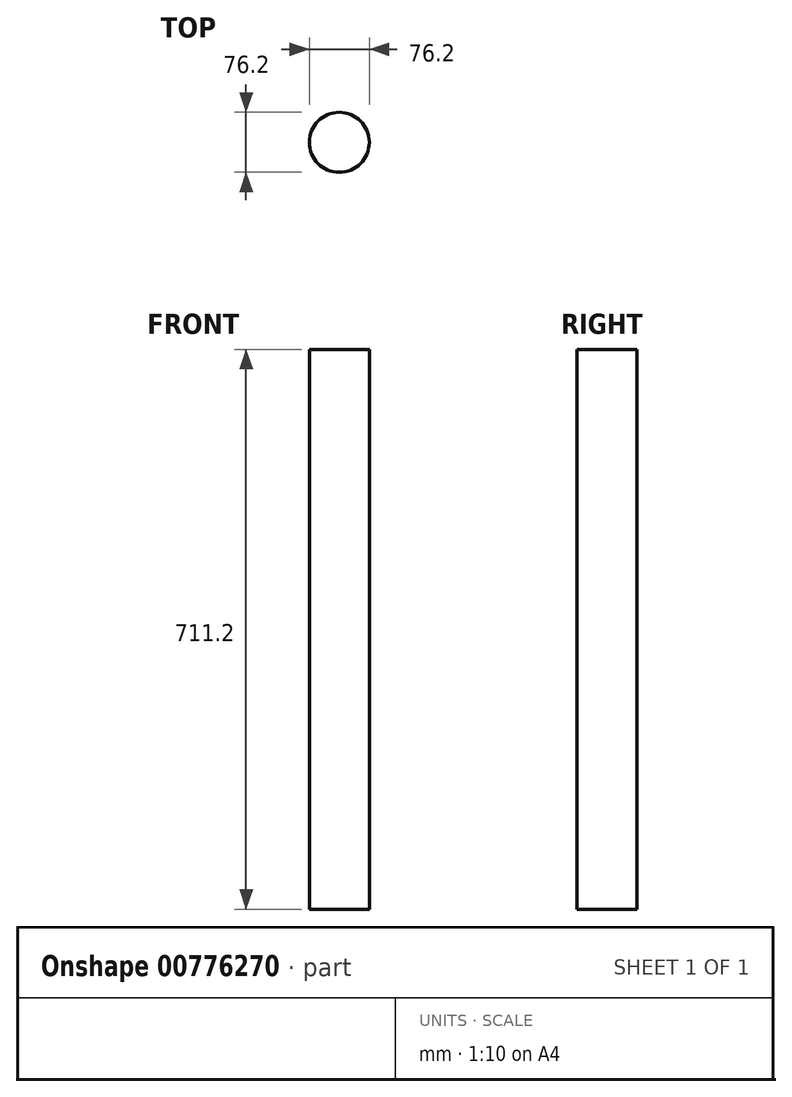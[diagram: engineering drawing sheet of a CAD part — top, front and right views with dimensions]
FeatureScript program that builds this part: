
annotation { "Feature Type Name" : "Feature", "Feature Type Description" : "" }
export const myFeature = defineFeature(function(context is Context, id is Id, definition is map)
    precondition{}
    {
        {
            var Q0;
            Q0=qCreatedBy(makeId("Top.planeOp"),FACE);
            var sketch = newSketch(context, id + "F0", { "sketchPlane" : qUnion([Q0])});
            skCircle(sketch, "E0", {"center": v(0, 0) * mm, "radius": 38.1 * mm});
            skSolve(sketch);
        }
        {
            var Q0;
            Q0 = qSketchRegion(id + "F0", true);
            extrude(context, id + "F1", {"entities" : qUnion([Q0]), "depth" : 711.2 * mm, "offsetDistance" : 25.4 * mm});
        }
    });
